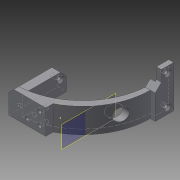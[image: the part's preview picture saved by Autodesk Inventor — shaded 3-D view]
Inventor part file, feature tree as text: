
AUTODESK INVENTOR PART (.ipt)
format: ipt  version: 2015 (Build 190159000, 159)  size: 297,984 bytes
history: native  units: mm
features: sketch x23, extrude x16, hole x4, chamfer x4, fillet x1, plane x1
ambient origin geometry x8: Origin, YZ Plane, XZ Plane, XY Plane, X Axis, Y Axis, Z Axis, Center Point
bodies: Solid1 (feature_tree)
feature tree (49):
  extrude  "Extrusion1"  Depth=40.0mm
  hole  "Hole1"  [1 undecoded]
  extrude  "Extrusion2"  Depth=3.0mm
  extrude  "Extrusion3"  Depth=4.0mm
  extrude  "Extrusion8"  Depth=10.0mm TaperAngle=0.0deg
  extrude  "Extrusion9"  Depth=23.0mm
  sketch  "Sketch12"  dims[d21=5.0mm d22=23.0mm]
  extrude  "Extrusion10"  Depth=5.0mm
  sketch  "Sketch14"  dims[d25=4.0mm d26=0.0mm d40=10.0mm d41=0.0mm]
  extrude  "Extrusion11"  Depth=10.0mm TaperAngle=0.0deg
  extrude  "Extrusion12"  Depth=10.0mm
  extrude  "Extrusion13"  Depth=4.0mm
  hole  "Hole3"  [1 undecoded]
  fillet  "Fillet4"  Radius=4.0mm
  chamfer  "Chamfer2"  Distance=20.0mm
  chamfer  "Chamfer3"  Distance=6.0mm
  extrude  "Extrusion14"  Depth=5.0mm
  extrude  "Extrusion15"  Depth=55.0mm
  chamfer  "Chamfer4"  Distance=4.0mm Angle=45.0deg
  extrude  "Extrusion16"  Depth=4.0mm TaperAngle=0.0deg
  chamfer  "Chamfer5"  Distance=4.0mm
  hole  "Hole4"  [1 undecoded]
  extrude  "Extrusion17"  Depth=1.0mm
  sketch  "Sketch24"  dims[d95=5.0mm d96=5.0mm]
  plane  "Work Plane1"
  extrude  "Extrusion18"  Depth=5.0mm
  extrude  "Extrusion19"  Depth=1.0mm TaperAngle=0.0deg
  hole  "Hole5"  [1 undecoded]
  extrude  "Extrusion20"  Depth=1.0mm
  sketch  "Sketch1"  dims[d0=7.0mm d1=40.0mm]
  sketch  "Sketch2"  dims[d2=10.0mm d3=0.0mm d4=5.0mm]
  sketch  "Sketch3"  dims[d5=5.0mm]
  sketch  "Sketch4"  dims[d6=3.0mm d7=6.0mm d8=6.0mm d9=2.0mm d10=90.0deg d11=8.0mm d12=20.594885mm d13=60.0mm]
  sketch  "Sketch9"  dims[d14=4.0mm d15=4.0mm]
  sketch  "Sketch10"  dims[d16=65.0mm d17=10.0mm d18=0.0mm]
  sketch  "Sketch13"  dims[d23=11.0mm d24=5.0mm]
  sketch  "Sketch15"  dims[d42=10.0mm d43=0.0mm d53=60.0mm]
  sketch  "Sketch16"  dims[d54=4.0mm d55=4.0mm]
  sketch  "Sketch17"  dims[d56=6.0mm d57=0.0mm d58=20.0mm d59=0.0mm d60=4.0mm]
  sketch  "Sketch18"  dims[d61=4.0mm d62=20.0mm d63=0.0mm d64=6.0mm d65=0.0mm]
  sketch  "Sketch19"  dims[d66=5.0mm d67=5.0mm]
  sketch  "Sketch20"  dims[d68=3.0mm d69=6.0mm d70=6.0mm d71=2.0mm d72=90.0deg d73=8.0mm d74=20.594885mm d75=55.0mm d76=4.0mm d77=2.0mm d78=45.0deg]
  sketch  "Sketch21"  dims[d79=5.0mm d80=2.0mm d81=45.0deg d82=4.0mm d83=0.0mm d84=4.0mm d85=0.0mm]
  sketch  "Sketch22"  dims[d86=5.0mm d87=2.0mm d88=45.0deg d89=4.0mm d90=0.0mm]
  sketch  "Sketch23"  dims[d91=1.0mm d92=2.0mm d93=45.0deg d94=5.0mm]
  sketch  "Sketch25"  dims[d97=5.0mm]
  sketch  "Sketch26"  dims[d98=3.0mm d99=6.0mm d100=6.0mm d101=2.0mm d102=90.0deg d103=8.0mm d104=20.594885mm d105=1.0mm d106=0.0mm]
  sketch  "Sketch27"  dims[d107=-45.0mm d108=10.0mm]
  sketch  "Sketch28"  dims[d109=50.0mm d110=0.0mm d111=25.0mm d112=4.0mm d113=5.0mm d114=3.0mm d115=20.0mm d116=0.0mm d117=5.0mm d118=5.0mm d119=5.0mm d120=5.0mm d121=10.0mm d122=3.0mm d123=6.0mm d124=6.0mm d125=2.0mm d126=90.0deg d127=6.0mm d128=20.594885mm d129=1.0mm d130=0.0mm]
note: 4 required parameter values undecoded (feature->parameter linkage not recoverable at this tier; creation-order binding heuristic only, values carry confidence <= 0.55)
